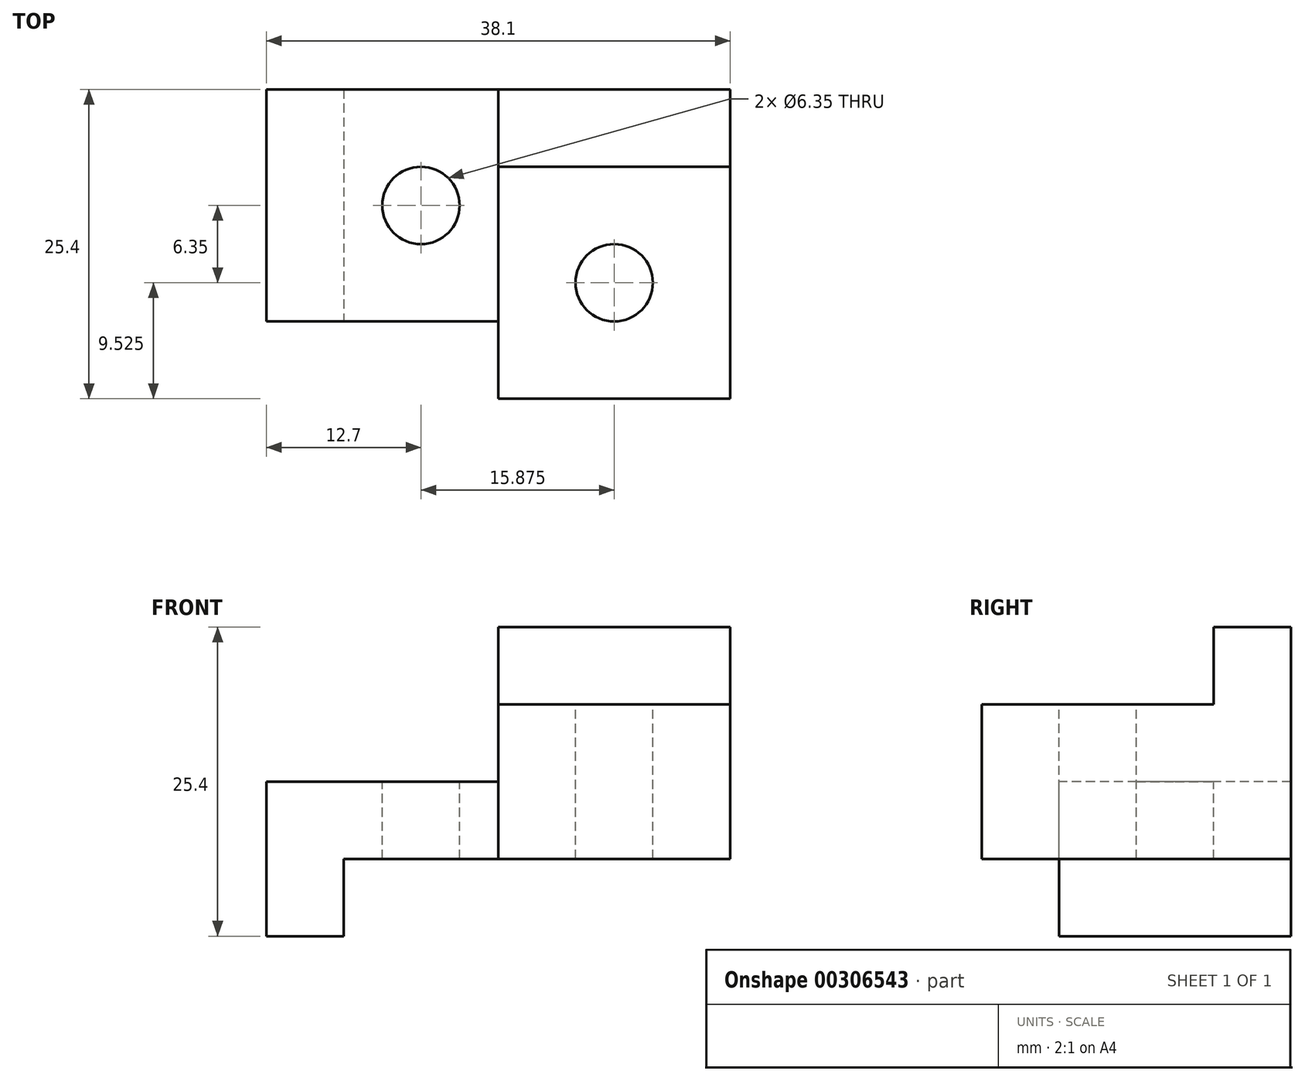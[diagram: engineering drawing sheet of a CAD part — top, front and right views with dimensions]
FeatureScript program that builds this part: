
annotation { "Feature Type Name" : "Feature", "Feature Type Description" : "" }
export const myFeature = defineFeature(function(context is Context, id is Id, definition is map)
    precondition{}
    {
        {
            var Q0;
            Q0=qCreatedBy(makeId("Front.planeOp"),FACE);
            var sketch = newSketch(context, id + "F0", { "sketchPlane" : qUnion([Q0])});
            skLineSegment(sketch, "E0.bottom", {"start": v(0, 0) * mm, "end": v(38.1, 0) * mm});
            skLineSegment(sketch, "E0.top", {"start": v(0, 25.4) * mm, "end": v(38.1, 25.4) * mm});
            skLineSegment(sketch, "E0.left", {"start": v(0, 0) * mm, "end": v(0, 25.4) * mm});
            skLineSegment(sketch, "E0.right", {"start": v(38.1, 0) * mm, "end": v(38.1, 25.4) * mm});
            skSolve(sketch);
        }
        {
            var Q0;
            Q0 = qSketchRegion(id + "F0", true);
            extrude(context, id + "F1", {"entities" : qUnion([Q0]), "depth" : 25.4 * mm});
        }
        {
            var Q0;
            Q0=makeQuery(id+"F1.opExtrude","CAP_FACE",FACE,{"disambiguationData":[OSD([sQuery(id+"F0.wireOp",EDGE,"E0.bottom"),sQuery(id+"F0.wireOp",EDGE,"E0.top"),sQuery(id+"F0.wireOp",EDGE,"E0.left"),sQuery(id+"F0.wireOp",EDGE,"E0.right")])],"isStart":false});
            var sketch = newSketch(context, id + "F2", { "sketchPlane" : qUnion([Q0])});
            skLineSegment(sketch, "E1.bottom", {"start": v(0, 25.4) * mm, "end": v(19.05, 25.4) * mm});
            skLineSegment(sketch, "E1.top", {"start": v(0, 12.7) * mm, "end": v(19.05, 12.7) * mm});
            skLineSegment(sketch, "E1.left", {"start": v(0, 25.4) * mm, "end": v(0, 12.7) * mm});
            skLineSegment(sketch, "E1.right", {"start": v(19.05, 25.4) * mm, "end": v(19.05, 12.7) * mm});
            skLineSegment(sketch, "E2.bottom", {"start": v(6.35, 0) * mm, "end": v(38.1, 0) * mm});
            skLineSegment(sketch, "E2.top", {"start": v(6.35, 6.35) * mm, "end": v(38.1, 6.35) * mm});
            skLineSegment(sketch, "E2.left", {"start": v(6.35, 0) * mm, "end": v(6.35, 6.35) * mm});
            skLineSegment(sketch, "E2.right", {"start": v(38.1, 0) * mm, "end": v(38.1, 6.35) * mm});
            skSolve(sketch);
        }
        {
            var Q0;
            Q0 = qSketchRegion(id + "F2", true);
            extrude(context, id + "F3", {"entities" : qUnion([Q0]), "operationType" : NewBodyOperationType.REMOVE, "endBound" : BoundingType.THROUGH_ALL, "oppositeDirection" : true, "depth" : 25.4 * mm});
        }
        {
            var Q0;
            Q0=makeQuery(id+"F3.boolean.opBoolean","COPY",FACE,{"derivedFrom":makeQuery(id+"F3.opExtrude","SWEPT_FACE",FACE,{"disambiguationData":[OSD([sQuery(id+"F2.wireOp",EDGE,"E1.top")])]})});
            var sketch = newSketch(context, id + "F4", { "sketchPlane" : qUnion([Q0])});
            skLineSegment(sketch, "E3.bottom", {"start": v(0, -25.4) * mm, "end": v(19.05, -25.4) * mm});
            skLineSegment(sketch, "E3.top", {"start": v(0, -19.05) * mm, "end": v(19.05, -19.05) * mm});
            skLineSegment(sketch, "E3.left", {"start": v(0, -25.4) * mm, "end": v(0, -19.05) * mm});
            skLineSegment(sketch, "E3.right", {"start": v(19.05, -25.4) * mm, "end": v(19.05, -19.05) * mm});
            skCircle(sketch, "E4", {"center": v(12.7, -9.53) * mm, "radius": 3.18 * mm});
            skSolve(sketch);
        }
        {
            var Q0;
            Q0 = qSketchRegion(id + "F4", true);
            extrude(context, id + "F5", {"entities" : qUnion([Q0]), "operationType" : NewBodyOperationType.REMOVE, "endBound" : BoundingType.THROUGH_ALL, "oppositeDirection" : true, "depth" : 25.4 * mm});
        }
        {
            var Q0;
            Q0=makeQuery(id+"F1.opExtrude","SWEPT_FACE",FACE,{"disambiguationData":[OSD([sQuery(id+"F0.wireOp",EDGE,"E0.top")])]});
            var sketch = newSketch(context, id + "F6", { "sketchPlane" : qUnion([Q0])});
            skLineSegment(sketch, "E5.bottom", {"start": v(19.05, -25.4) * mm, "end": v(38.1, -25.4) * mm});
            skLineSegment(sketch, "E5.top", {"start": v(19.05, -6.35) * mm, "end": v(38.1, -6.35) * mm});
            skLineSegment(sketch, "E5.left", {"start": v(19.05, -25.4) * mm, "end": v(19.05, -6.35) * mm});
            skLineSegment(sketch, "E5.right", {"start": v(38.1, -25.4) * mm, "end": v(38.1, -6.35) * mm});
            skSolve(sketch);
        }
        {
            var Q0;
            Q0 = qSketchRegion(id + "F6", true);
            extrude(context, id + "F7", {"entities" : qUnion([Q0]), "operationType" : NewBodyOperationType.REMOVE, "oppositeDirection" : true, "depth" : 6.35 * mm});
        }
        {
            var Q0;
            Q0=makeQuery(id+"F7.boolean.opBoolean","COPY",FACE,{"derivedFrom":makeQuery(id+"F7.opExtrude","CAP_FACE",FACE,{"disambiguationData":[OSD([sQuery(id+"F6.wireOp",EDGE,"E5.bottom"),sQuery(id+"F6.wireOp",EDGE,"E5.top"),sQuery(id+"F6.wireOp",EDGE,"E5.left"),sQuery(id+"F6.wireOp",EDGE,"E5.right")])],"isStart":false})});
            var sketch = newSketch(context, id + "F8", { "sketchPlane" : qUnion([Q0])});
            skCircle(sketch, "E6", {"center": v(28.57, -15.88) * mm, "radius": 3.17 * mm});
            skLineSegment(sketch, "E7", {"start": v(28.57, -15.88) * mm, "end": v(35.9, -15.88) * mm, "construction": true});
            skLineSegment(sketch, "E8", {"start": v(28.57, -15.88) * mm, "end": v(28.57, -9.14) * mm, "construction": true});
            skSolve(sketch);
        }
        {
            var Q0;
            Q0 = qSketchRegion(id + "F8", true);
            extrude(context, id + "F9", {"entities" : qUnion([Q0]), "operationType" : NewBodyOperationType.REMOVE, "endBound" : BoundingType.THROUGH_ALL, "oppositeDirection" : true, "depth" : 25.4 * mm});
        }
    });
